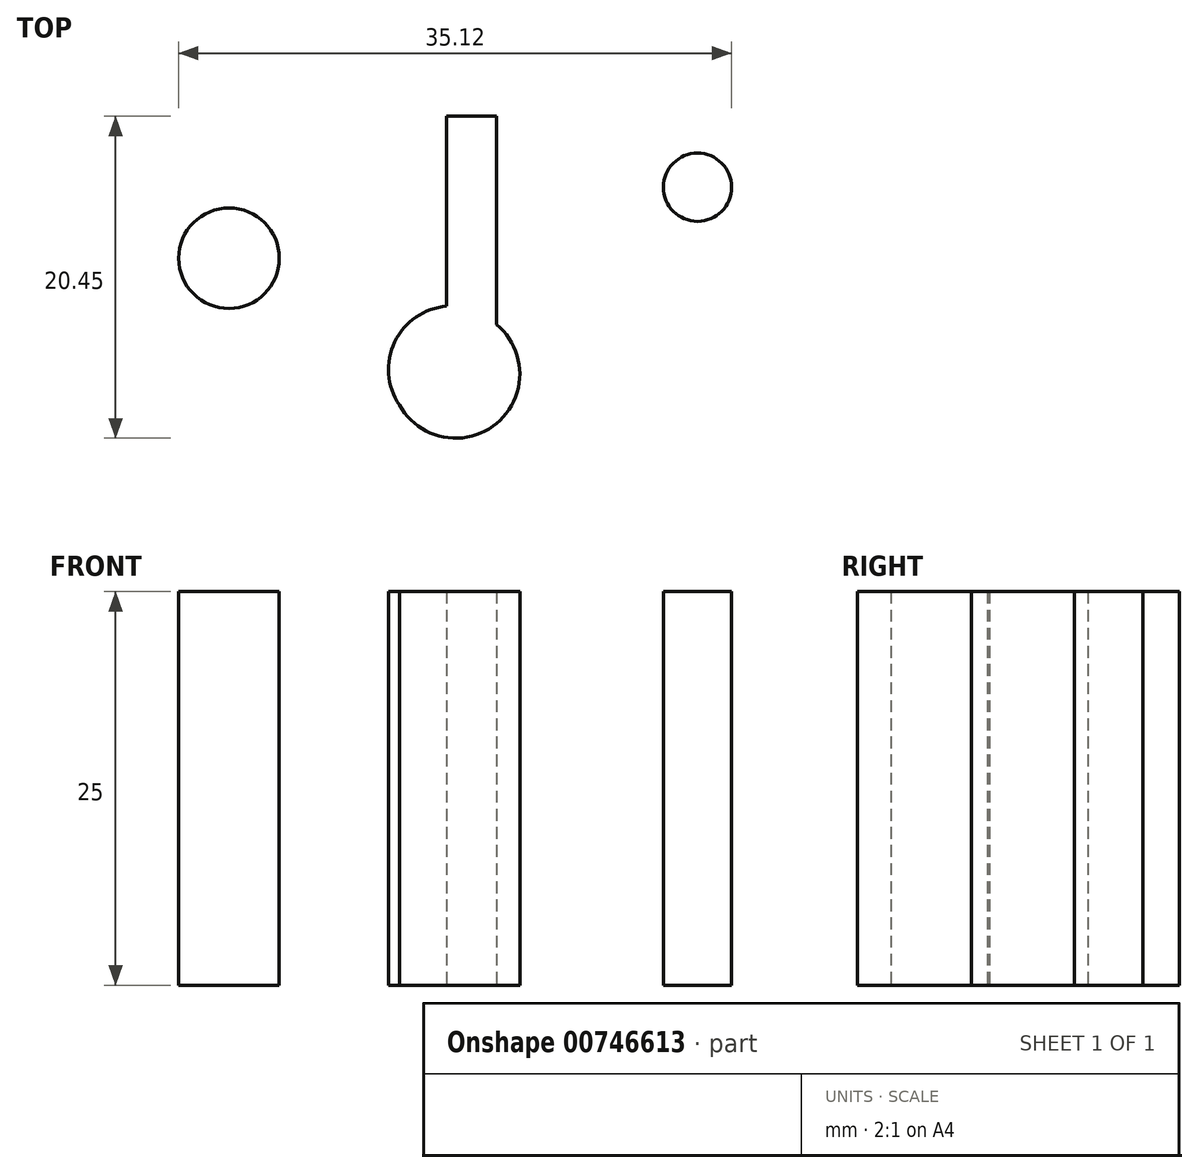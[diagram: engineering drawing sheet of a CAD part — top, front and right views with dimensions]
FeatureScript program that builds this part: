
annotation { "Feature Type Name" : "Feature", "Feature Type Description" : "" }
export const myFeature = defineFeature(function(context is Context, id is Id, definition is map)
    precondition{}
    {
        {
            var Q0;
            Q0=qCreatedBy(makeId("Top.planeOp"),FACE);
            var sketch = newSketch(context, id + "F0", { "sketchPlane" : qUnion([Q0])});
            skArc(sketch, "E0", {"start": v(25.4, 5.26) * mm, "mid": v(31.4, 19.86) * mm, "end": v(23, 33.21) * mm});
            skCircle(sketch, "E1", {"center": v(12.77, 26.6) * mm, "radius": 2.17 * mm});
            skArc(sketch, "E2", {"start": v(18.79, 32.61) * mm, "mid": v(12.84, 35.52) * mm, "end": v(6.76, 32.91) * mm});
            skArc(sketch, "E3", {"start": v(-4.96, 6.16) * mm, "mid": v(2.42, 2.6) * mm, "end": v(8.87, 7.66) * mm});
            skLineSegment(sketch, "E4", {"start": v(0, 31.1) * mm, "end": v(0, 17.88) * mm});
            skArc(sketch, "E5", {"start": v(0, 17.88) * mm, "mid": v(-5.4, 18.12) * mm, "end": v(-6.16, 12.77) * mm});
            skArc(sketch, "E6", {"start": v(-6.16, 12.77) * mm, "mid": v(0.01, 11.6) * mm, "end": v(0, 17.88) * mm});
            skLineSegment(sketch, "E7", {"start": v(0, 31.1) * mm, "end": v(-3.16, 31.1) * mm});
            skLineSegment(sketch, "E8", {"start": v(-3.16, 31.1) * mm, "end": v(-3.16, 19.04) * mm});
            skArc(sketch, "E9", {"start": v(-31.4, 36.22) * mm, "mid": v(-37.04, 19.34) * mm, "end": v(-31.1, 2.55) * mm});
            skCircle(sketch, "E10", {"center": v(-16.98, 22.1) * mm, "radius": 3.2 * mm});
            skArc(sketch, "E11", {"start": v(-10.97, 29.3) * mm, "mid": v(-14.97, 34.17) * mm, "end": v(-20.89, 32.01) * mm});
            skSolve(sketch);
        }
        {
            var Q0;
            Q0=makeQuery(id+"F0.imprint","IMPRINT",FACE,{"disambiguationData":[TD([[makeQuery(id+"F0.imprint","IMPRINT",EDGE,{"derivedFrom":sQuery(id+"F0.wireOp",EDGE,"E10")}),1.0]])]});
            var Q1;
            Q1=makeQuery(id+"F0.imprint","IMPRINT",FACE,{"disambiguationData":[TD([[makeQuery(id+"F0.imprint","IMPRINT",EDGE,{"derivedFrom":sQuery(id+"F0.wireOp",EDGE,"E1")}),1.0]])]});
            var Q2;
            {var subQ0=sQuery(id+"F0.wireOp",EDGE,"E6");Q2=makeQuery(id+"F0.imprint","IMPRINT",FACE,{"disambiguationData":[TD([[makeQuery(id+"F0.imprint","IMPRINT",EDGE,{"derivedFrom":subQ0}),1.0]])]});}
            var Q3;
            {var subQ0=sQuery(id+"F0.wireOp",EDGE,"E4");Q3=makeQuery(id+"F0.imprint","IMPRINT",FACE,{"disambiguationData":[TD([[makeQuery(id+"F0.imprint","IMPRINT",EDGE,{"derivedFrom":subQ0}),-1.0]])]});}
            extrude(context, id + "F1", {"entities" : qUnion([Q0, Q1, Q2, Q3]), "depth" : 25 * mm, "offsetDistance" : 25 * mm});
        }
    });
